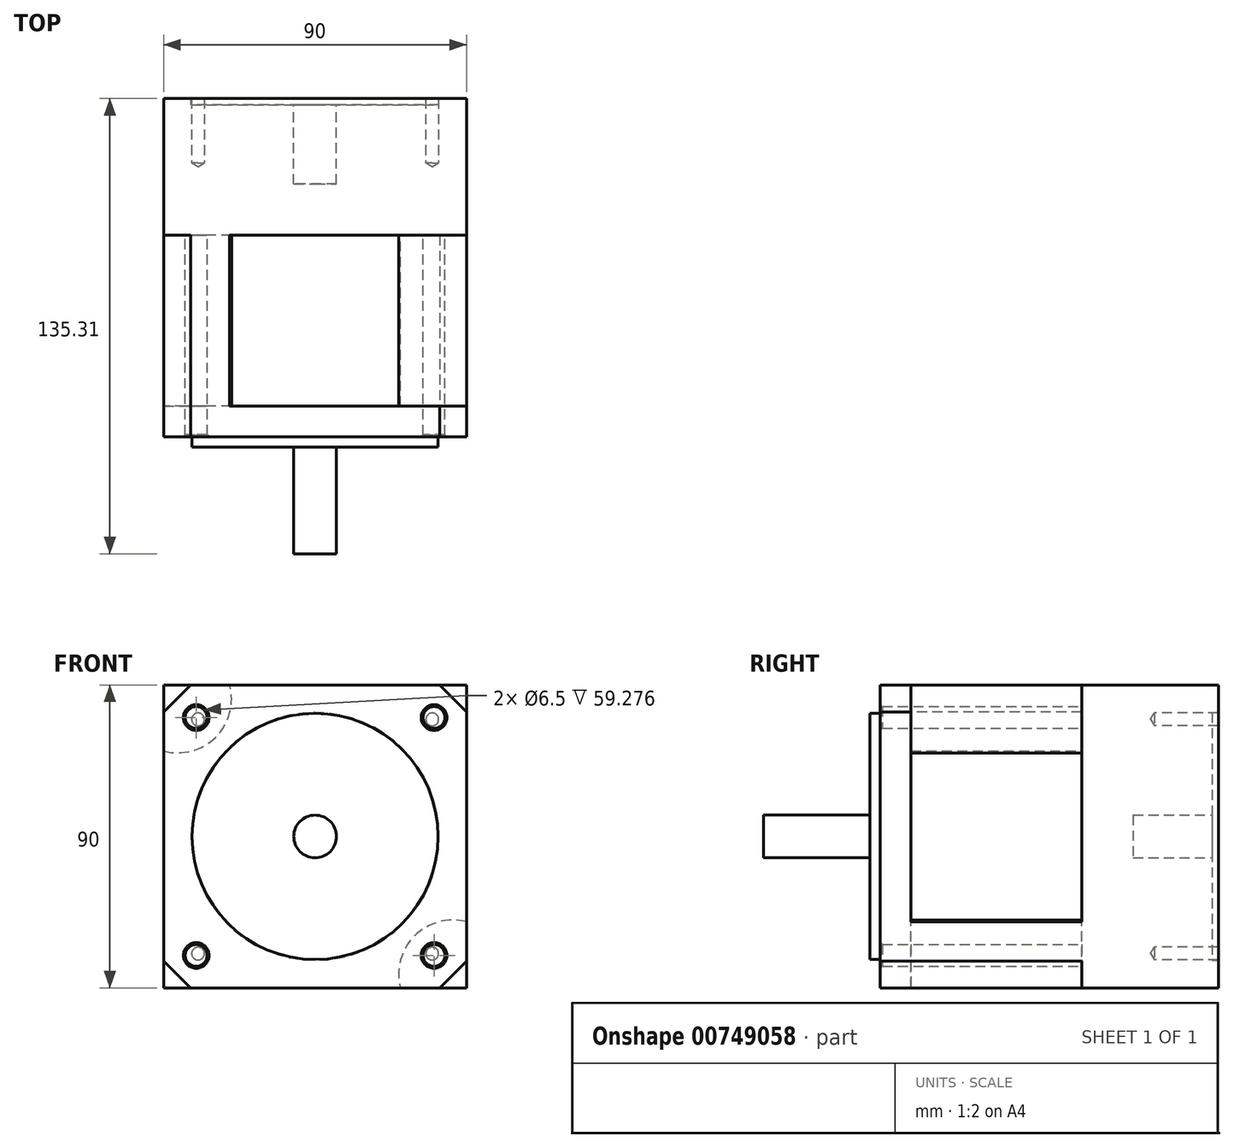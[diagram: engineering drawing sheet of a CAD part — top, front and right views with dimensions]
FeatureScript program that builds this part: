
annotation { "Feature Type Name" : "Feature", "Feature Type Description" : "" }
export const myFeature = defineFeature(function(context is Context, id is Id, definition is map)
    precondition{}
    {
        {
            var Q0;
            Q0=qCreatedBy(makeId("Front.planeOp"),FACE);
            var sketch = newSketch(context, id + "F0", { "sketchPlane" : qUnion([Q0])});
            skLineSegment(sketch, "E0.bottom", {"start": v(37.03, 45) * mm, "end": v(-37.03, 45) * mm});
            skLineSegment(sketch, "E0.top", {"start": v(37.03, -45) * mm, "end": v(-37.03, -45) * mm});
            skLineSegment(sketch, "E0.left", {"start": v(45, 37.03) * mm, "end": v(45, -37.03) * mm});
            skLineSegment(sketch, "E0.right", {"start": v(-45, 37.03) * mm, "end": v(-45, -37.03) * mm});
            skPoint(sketch, "E0.middle", {"position": v(0, 0) * mm});
            skCircle(sketch, "E1", {"center": v(0, 0) * mm, "radius": 50 * mm, "construction": true});
            skLineSegment(sketch, "E2", {"start": v(-41.01, -41.01) * mm, "end": v(41.01, 41.01) * mm, "construction": true});
            skLineSegment(sketch, "E3", {"start": v(-41.01, 41.01) * mm, "end": v(41.01, -41.01) * mm, "construction": true});
            skPoint(sketch, "E4", {"position": v(-35.36, 35.36) * mm});
            skPoint(sketch, "E5", {"position": v(35.36, 35.36) * mm});
            skPoint(sketch, "E6", {"position": v(35.36, -35.36) * mm});
            skPoint(sketch, "E7", {"position": v(-35.36, -35.36) * mm});
            skLineSegment(sketch, "E8.MirrorCS", {"start": v(37.03, 45) * mm, "end": v(45, 37.03) * mm});
            skLineSegment(sketch, "E9.MirrorCS", {"start": v(-45, -37.03) * mm, "end": v(-37.03, -45) * mm});
            skLineSegment(sketch, "E10", {"start": v(0, 45) * mm, "end": v(0, -45) * mm, "construction": true});
            skLineSegment(sketch, "E11.MirrorCS", {"start": v(45, -37.03) * mm, "end": v(37.03, -45) * mm});
            skLineSegment(sketch, "E12.MirrorCS", {"start": v(-37.03, 45) * mm, "end": v(-45, 37.03) * mm});
            skSolve(sketch);
        }
        {
            var Q0;
            Q0 = qSketchRegion(id + "F0", true);
            extrude(context, id + "F1", {"entities" : qUnion([Q0]), "oppositeDirection" : true, "depth" : 59.92 * mm, "offsetDistance" : 25.4 * mm});
        }
        {
            var Q0;
            Q0=sQuery(id+"F0.wireOp",VERTEX,"E4");
            var Q1;
            Q1=sQuery(id+"F0.wireOp",VERTEX,"E7");
            var Q2;
            Q2=sQuery(id+"F0.wireOp",VERTEX,"E6");
            var Q3;
            Q3=sQuery(id+"F0.wireOp",VERTEX,"E5");
            var Q4;
            Q4=makeQuery(id+"F1.opExtrude","SWEPT_BODY",BODY,{"disambiguationData":[OSD([sQuery(id+"F0.wireOp",EDGE,"E0.bottom"),sQuery(id+"F0.wireOp",EDGE,"E0.top"),sQuery(id+"F0.wireOp",EDGE,"E0.left"),sQuery(id+"F0.wireOp",EDGE,"E0.right"),sQuery(id+"F0.wireOp",EDGE,"E8.MirrorCS"),sQuery(id+"F0.wireOp",EDGE,"E9.MirrorCS"),sQuery(id+"F0.wireOp",EDGE,"E11.MirrorCS"),sQuery(id+"F0.wireOp",EDGE,"E12.MirrorCS")])]});
            hole(context, id + "F2", {"style" : HoleStyle.C_SINK, "endStyle" : HoleEndStyle.BLIND, "holeDiameter" : 6.5 * mm, "cSinkDiameter" : 7.62 * mm, "cSinkAngle" : 82 * degree, "majorDiameter" : 9.52 * mm, "holeDepth" : 59.92 * mm, "isTappedThrough" : true, "tappedDepth" : 15.9 * mm, "tapClearance" : 3, "startFromSketch" : true, "locations" : qUnion([Q0, Q1, Q2, Q3]), "scope" : qUnion([Q4])});
        }
        {
            var Q0;
            Q0=makeQuery(id+"F1.opExtrude","CAP_FACE",FACE,{"disambiguationData":[OSD([sQuery(id+"F0.wireOp",EDGE,"E0.bottom"),sQuery(id+"F0.wireOp",EDGE,"E0.top"),sQuery(id+"F0.wireOp",EDGE,"E0.left"),sQuery(id+"F0.wireOp",EDGE,"E0.right"),sQuery(id+"F0.wireOp",EDGE,"E8.MirrorCS"),sQuery(id+"F0.wireOp",EDGE,"E9.MirrorCS"),sQuery(id+"F0.wireOp",EDGE,"E11.MirrorCS"),sQuery(id+"F0.wireOp",EDGE,"E12.MirrorCS")])],"isStart":false});
            var sketch = newSketch(context, id + "F3", { "sketchPlane" : qUnion([Q0])});
            skLineSegment(sketch, "E13", {"start": v(0, 45) * mm, "end": v(0, -45) * mm, "construction": true});
            skLineSegment(sketch, "E14", {"start": v(-45, 0) * mm, "end": v(45, 0) * mm, "construction": true});
            skPoint(sketch, "E15", {"position": v(-25.4, 45) * mm});
            skPoint(sketch, "E16", {"position": v(-45, 25.4) * mm});
            skArc(sketch, "E17", {"start": v(-45, 25.4) * mm, "mid": v(-29.54, 29.54) * mm, "end": v(-25.4, 45) * mm});
            skArc(sketch, "E18.MirrorCS", {"start": v(45, 25.4) * mm, "mid": v(29.54, 29.54) * mm, "end": v(25.4, 45) * mm});
            skArc(sketch, "E19.MirrorCS", {"start": v(-45, -25.4) * mm, "mid": v(-29.54, -29.54) * mm, "end": v(-25.4, -45) * mm});
            skArc(sketch, "E20.MirrorCS", {"start": v(45, -25.4) * mm, "mid": v(29.54, -29.54) * mm, "end": v(25.4, -45) * mm});
            skSolve(sketch);
        }
        {
            var Q0;
            Q0 = qSketchRegion(id + "F3", true);
            var Q1;
            {var subQ2=sQuery(id+"F3.wireOp",EDGE,"E17");Q1=makeQuery(id+"F3.imprint","IMPRINT",FACE,{"disambiguationData":[TD([[makeQuery(id+"F3.imprint","IMPRINT",EDGE,{"derivedFrom":subQ2}),1.0]])]});}
            var Q2;
            {var subQ2=sQuery(id+"F3.wireOp",EDGE,"E20.MirrorCS");Q2=makeQuery(id+"F3.imprint","IMPRINT",FACE,{"disambiguationData":[TD([[makeQuery(id+"F3.imprint","IMPRINT",EDGE,{"derivedFrom":subQ2}),1.0]])]});}
            var Q3;
            {var subQ2=sQuery(id+"F3.wireOp",EDGE,"E19.MirrorCS");Q3=makeQuery(id+"F3.imprint","IMPRINT",FACE,{"disambiguationData":[TD([[makeQuery(id+"F3.imprint","IMPRINT",EDGE,{"derivedFrom":subQ2}),-1.0]])]});}
            var Q4;
            {var subQ2=sQuery(id+"F3.wireOp",EDGE,"E18.MirrorCS");Q4=makeQuery(id+"F3.imprint","IMPRINT",FACE,{"disambiguationData":[TD([[makeQuery(id+"F3.imprint","IMPRINT",EDGE,{"derivedFrom":subQ2}),-1.0]])]});}
            extrude(context, id + "F4", {"entities" : qUnion([Q0, Q1, Q2, Q3, Q4]), "operationType" : NewBodyOperationType.REMOVE, "oppositeDirection" : true, "depth" : 50.8 * mm, "offsetDistance" : 25.4 * mm});
        }
        {
            var Q0;
            Q0=makeQuery(id+"F1.opExtrude","CAP_FACE",FACE,{"disambiguationData":[OSD([sQuery(id+"F0.wireOp",EDGE,"E0.bottom"),sQuery(id+"F0.wireOp",EDGE,"E0.top"),sQuery(id+"F0.wireOp",EDGE,"E0.left"),sQuery(id+"F0.wireOp",EDGE,"E0.right"),sQuery(id+"F0.wireOp",EDGE,"E8.MirrorCS"),sQuery(id+"F0.wireOp",EDGE,"E9.MirrorCS"),sQuery(id+"F0.wireOp",EDGE,"E11.MirrorCS"),sQuery(id+"F0.wireOp",EDGE,"E12.MirrorCS")])],"isStart":false});
            var sketch = newSketch(context, id + "F5", { "sketchPlane" : qUnion([Q0])});
            skLineSegment(sketch, "E21.bottom", {"start": v(45, -45) * mm, "end": v(-45, -45) * mm});
            skLineSegment(sketch, "E21.top", {"start": v(45, 45) * mm, "end": v(-45, 45) * mm});
            skLineSegment(sketch, "E21.left", {"start": v(45, -45) * mm, "end": v(45, 45) * mm});
            skLineSegment(sketch, "E21.right", {"start": v(-45, -45) * mm, "end": v(-45, 45) * mm});
            skPoint(sketch, "E21.middle", {"position": v(0, 0) * mm});
            skSolve(sketch);
        }
        {
            var Q0;
            Q0 = qSketchRegion(id + "F5", true);
            extrude(context, id + "F6", {"entities" : qUnion([Q0]), "operationType" : NewBodyOperationType.ADD, "depth" : 40.64 * mm, "offsetDistance" : 25.4 * mm});
        }
        {
            var Q0;
            Q0=makeQuery(id+"F6.opExtrude","CAP_FACE",FACE,{"disambiguationData":[OSD([sQuery(id+"F5.wireOp",EDGE,"E21.bottom"),sQuery(id+"F5.wireOp",EDGE,"E21.top"),sQuery(id+"F5.wireOp",EDGE,"E21.left"),sQuery(id+"F5.wireOp",EDGE,"E21.right")])],"isStart":false});
            var sketch = newSketch(context, id + "F7", { "sketchPlane" : qUnion([Q0])});
            skCircle(sketch, "E22", {"center": v(0, 0) * mm, "radius": 6.35 * mm});
            skSolve(sketch);
        }
        {
            var Q0;
            Q0 = qSketchRegion(id + "F7", true);
            extrude(context, id + "F8", {"entities" : qUnion([Q0]), "operationType" : NewBodyOperationType.REMOVE, "oppositeDirection" : true, "depth" : 25.4 * mm, "offsetDistance" : 25.4 * mm});
        }
        {
            var Q0;
            Q0=makeQuery(id+"F1.opExtrude","CAP_FACE",FACE,{"disambiguationData":[OSD([sQuery(id+"F0.wireOp",EDGE,"E0.bottom"),sQuery(id+"F0.wireOp",EDGE,"E0.top"),sQuery(id+"F0.wireOp",EDGE,"E0.left"),sQuery(id+"F0.wireOp",EDGE,"E0.right"),sQuery(id+"F0.wireOp",EDGE,"E8.MirrorCS"),sQuery(id+"F0.wireOp",EDGE,"E9.MirrorCS"),sQuery(id+"F0.wireOp",EDGE,"E11.MirrorCS"),sQuery(id+"F0.wireOp",EDGE,"E12.MirrorCS")])],"isStart":true});
            var sketch = newSketch(context, id + "F9", { "sketchPlane" : qUnion([Q0])});
            skCircle(sketch, "E23", {"center": v(0, 0) * mm, "radius": 36.58 * mm});
            skSolve(sketch);
        }
        {
            var Q0;
            Q0 = qSketchRegion(id + "F9", true);
            extrude(context, id + "F10", {"entities" : qUnion([Q0]), "operationType" : NewBodyOperationType.ADD, "depth" : 3 * mm, "offsetDistance" : 25.4 * mm});
        }
        {
            var Q0;
            Q0=makeQuery(id+"F10.opExtrude","CAP_FACE",FACE,{"disambiguationData":[OSD([sQuery(id+"F9.wireOp",EDGE,"E23")])],"isStart":false});
            var sketch = newSketch(context, id + "F11", { "sketchPlane" : qUnion([Q0])});
            skCircle(sketch, "E24", {"center": v(0, 0) * mm, "radius": 6.35 * mm});
            skSolve(sketch);
        }
        {
            var Q0;
            Q0 = qSketchRegion(id + "F11", true);
            extrude(context, id + "F12", {"entities" : qUnion([Q0]), "operationType" : NewBodyOperationType.ADD, "depth" : 31.75 * mm, "offsetDistance" : 25.4 * mm});
        }
        {
            var Q0;
            Q0=makeQuery(id+"F6.opExtrude","CAP_FACE",FACE,{"disambiguationData":[OSD([sQuery(id+"F5.wireOp",EDGE,"E21.bottom"),sQuery(id+"F5.wireOp",EDGE,"E21.top"),sQuery(id+"F5.wireOp",EDGE,"E21.left"),sQuery(id+"F5.wireOp",EDGE,"E21.right")])],"isStart":false});
            var sketch = newSketch(context, id + "F13", { "sketchPlane" : qUnion([Q0])});
            skLineSegment(sketch, "E25", {"start": v(-45, 45) * mm, "end": v(45, -45) * mm, "construction": true});
            skLineSegment(sketch, "E26", {"start": v(45, 45) * mm, "end": v(-45, -45) * mm, "construction": true});
            skCircle(sketch, "E27", {"center": v(0, 0) * mm, "radius": 49.23 * mm, "construction": true});
            skPoint(sketch, "E28", {"position": v(-34.8, 34.8) * mm});
            skPoint(sketch, "E29", {"position": v(34.8, 34.8) * mm});
            skPoint(sketch, "E30", {"position": v(34.8, -34.8) * mm});
            skPoint(sketch, "E31", {"position": v(-34.8, -34.8) * mm});
            skCircle(sketch, "E32", {"center": v(0, 0) * mm, "radius": 36.83 * mm});
            skSolve(sketch);
        }
        {
            var Q0;
            Q0=sQuery(id+"F13.wireOp",VERTEX,"E28");
            var Q1;
            Q1=sQuery(id+"F13.wireOp",VERTEX,"E31");
            var Q2;
            Q2=sQuery(id+"F13.wireOp",VERTEX,"E30");
            var Q3;
            Q3=sQuery(id+"F13.wireOp",VERTEX,"E29");
            var Q4;
            Q4=makeQuery(id+"F1.opExtrude","SWEPT_BODY",BODY,{"disambiguationData":[OSD([sQuery(id+"F0.wireOp",EDGE,"E0.bottom"),sQuery(id+"F0.wireOp",EDGE,"E0.top"),sQuery(id+"F0.wireOp",EDGE,"E0.left"),sQuery(id+"F0.wireOp",EDGE,"E0.right"),sQuery(id+"F0.wireOp",EDGE,"E8.MirrorCS"),sQuery(id+"F0.wireOp",EDGE,"E9.MirrorCS"),sQuery(id+"F0.wireOp",EDGE,"E11.MirrorCS"),sQuery(id+"F0.wireOp",EDGE,"E12.MirrorCS")])]});
            hole(context, id + "F14", {"style" : HoleStyle.SIMPLE, "endStyle" : HoleEndStyle.BLIND, "standardTappedOrClearance" : lookupTablePath({ "standard" : "ANSI", "engagement" : "75%", "pitch" : "24 tpi", "size" : "#10", "type" : "Tapped" }), "standardBlindInLast" : lookupTablePath({ "standard" : "ANSI", "engagement" : "75%", "pitch" : "24 tpi", "size" : "#10", "type" : "Tapped" }), "holeDiameter" : 3.8 * mm, "majorDiameter" : 4.83 * mm, "showTappedDepth" : true, "holeDepth" : 19.1 * mm, "isTappedThrough" : true, "tappedDepth" : 15.93 * mm, "tapClearance" : 3, "startFromSketch" : true, "locations" : qUnion([Q0, Q1, Q2, Q3]), "scope" : qUnion([Q4])});
        }
        {
            var Q0;
            Q0 = qSketchRegion(id + "F13", true);
            extrude(context, id + "F15", {"entities" : qUnion([Q0]), "operationType" : NewBodyOperationType.REMOVE, "oppositeDirection" : true, "depth" : 1.9 * mm, "offsetDistance" : 25.4 * mm});
        }
    });
